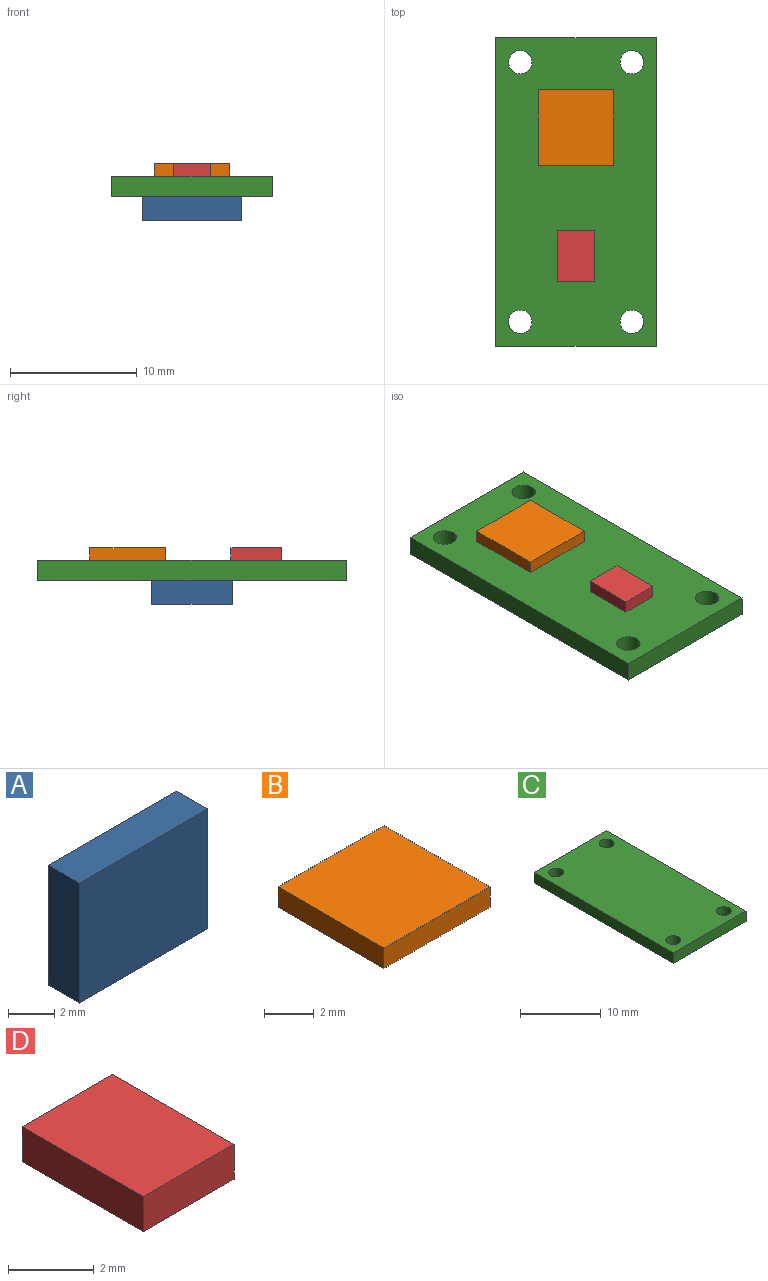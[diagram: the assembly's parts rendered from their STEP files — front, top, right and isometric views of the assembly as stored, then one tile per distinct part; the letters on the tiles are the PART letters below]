
ASSEMBLY  parts=4 mates=3
PART A: 6 faces, bbox 7.9x1.9x6.4 mm
  f0: plane 6.35x1.91mm, normal (1,0,0), area 12.1mm2, adj f1,f3,f4,f5
  f1: plane 7.87x1.91mm, normal (0,0,-1), area 15mm2, adj f0,f2,f4,f5
  f2: plane 6.35x1.91mm, normal (-1,0,0), area 12.1mm2, adj f1,f3,f4,f5
  f3: plane 7.87x1.91mm, normal (0,0,1), area 15mm2, adj f0,f2,f4,f5
  f4: plane 7.87x6.35mm, normal (0,1,0), area 50mm2, adj f0,f1,f2,f3
  f5: plane 7.87x6.35mm, normal (0,-1,0), area 50mm2, adj f0,f1,f2,f3
PART B: 6 faces, bbox 6x6x1 mm
  f0: plane 6x1mm, normal (1,0,0), area 6mm2, adj f1,f3,f4,f5
  f1: plane 6x1mm, normal (0,1,0), area 6mm2, adj f0,f2,f4,f5
  f2: plane 6x1mm, normal (-1,0,0), area 6mm2, adj f1,f3,f4,f5
  f3: plane 6x1mm, normal (0,-1,0), area 6mm2, adj f0,f2,f4,f5
  f4: plane 6x6mm, normal (0,0,1), area 36mm2, adj f0,f1,f2,f3
  f5: plane 6x6mm, normal (0,0,-1), area 36mm2, adj f0,f1,f2,f3
PART C: 10 faces, bbox 12.7x24.4x1.6 mm
  f0: plane 24.38x1.59mm, normal (1,0,0), area 38.7mm2, adj f1,f5,f8,f9
  f1: plane 12.7x1.59mm, normal (0,-1,0), area 20.2mm2, adj f0,f2,f8,f9
  f2: plane 24.38x1.59mm, normal (-1,0,0), area 38.7mm2, adj f1,f5,f8,f9
  f3: cylinder r=0.93mm len=1.85mm, axis (0,0,1), area 9.2mm2, adj f8,f9
  f4: cylinder r=0.93mm len=1.85mm, axis (0,0,1), area 9.2mm2, adj f8,f9
  f5: plane 12.7x1.59mm, normal (0,1,0), area 20.2mm2, adj f0,f2,f8,f9
  f6: cylinder r=0.93mm len=1.85mm, axis (0,0,1), area 9.2mm2, adj f8,f9
  f7: cylinder r=0.93mm len=1.85mm, axis (0,0,1), area 9.2mm2, adj f8,f9
  f8: plane 24.38x12.7mm, normal (0,0,-1), area 298.9mm2, adj f0,f1,f2,f3,f4,f5,f6,f7
  f9: plane 24.38x12.7mm, normal (0,0,1), area 298.9mm2, adj f0,f1,f2,f3,f4,f5,f6,f7
PART D: 6 faces, bbox 3x4x1 mm
  f0: plane 4x1mm, normal (1,0,0), area 4mm2, adj f1,f3,f4,f5
  f1: plane 3x1mm, normal (0,1,0), area 3mm2, adj f0,f2,f4,f5
  f2: plane 4x1mm, normal (-1,0,0), area 4mm2, adj f1,f3,f4,f5
  f3: plane 3x1mm, normal (0,-1,0), area 3mm2, adj f0,f2,f4,f5
  f4: plane 4x3mm, normal (0,0,1), area 12mm2, adj f0,f1,f2,f3
  f5: plane 4x3mm, normal (0,0,-1), area 12mm2, adj f0,f1,f2,f3
PLACE A rot(axis=(-1,0,0),90deg) t=(0,0,-1.59)mm
PLACE B rot(axis=(1,0,0),180deg) t=(0,5.08,1)mm
PLACE C t=(0,0,2.9)mm
PLACE D rot(axis=(1,0,0),180deg) t=(0,-5.08,1)mm
MATE fastened D.f4 <-> C.f9  axis (0,0,-1) through (0,-5.08,0)mm
MATE fastened A.f5 <-> C.f8  axis (0,0,1) through (0,0,-1.59)mm
MATE fastened B.f4 <-> C.f9  axis (0,0,-1) through (0,5.08,0)mm
